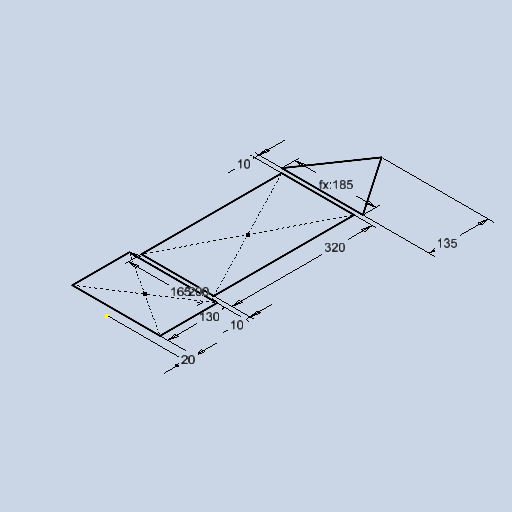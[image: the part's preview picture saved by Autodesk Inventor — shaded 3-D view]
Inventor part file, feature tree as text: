
AUTODESK INVENTOR PART (.ipt)
format: ipt  version: 2025 (Build 290162010, 162A)  size: 86,528 bytes
history: native  units: mm
features: sketch x1
ambient origin geometry x8: Origin, YZ Plane, XZ Plane, XY Plane, X Axis, Y Axis, Z Axis, Center Point
feature tree (1):
  sketch  "Sketch1"  dims[d0=200.0mm d1=130.0mm d2=320.0mm d3=165.0mm d4=20.0mm d5=10.0mm d6=135.0mm d7=10.0mm d8=185.0mm]
